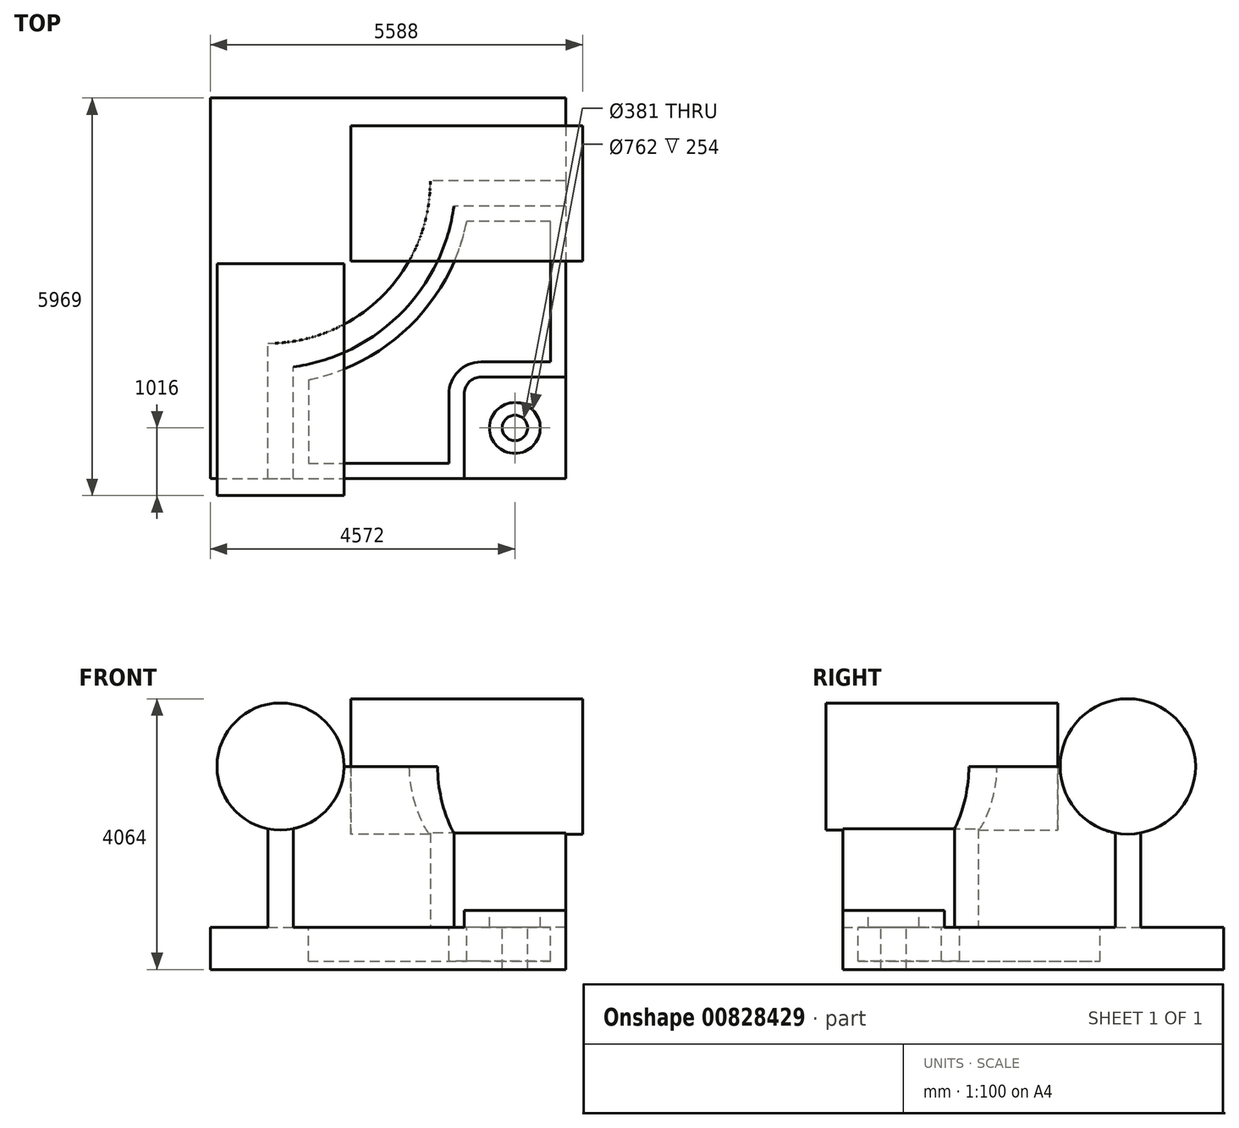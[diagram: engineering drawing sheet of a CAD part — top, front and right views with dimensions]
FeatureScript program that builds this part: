
annotation { "Feature Type Name" : "Feature", "Feature Type Description" : "" }
export const myFeature = defineFeature(function(context is Context, id is Id, definition is map)
    precondition{}
    {
        {
            var Q0;
            Q0=qCreatedBy(makeId("Top.planeOp"),FACE);
            var sketch = newSketch(context, id + "F0", { "sketchPlane" : qUnion([Q0])});
            skLineSegment(sketch, "E0.bottom", {"start": v(-2667, 2857.5) * mm, "end": v(2667, 2857.5) * mm});
            skLineSegment(sketch, "E0.top", {"start": v(-2667, -2857.5) * mm, "end": v(2667, -2857.5) * mm});
            skLineSegment(sketch, "E0.left", {"start": v(-2667, 2857.5) * mm, "end": v(-2667, -2857.5) * mm});
            skLineSegment(sketch, "E0.right", {"start": v(2667, 2857.5) * mm, "end": v(2667, -2857.5) * mm});
            skPoint(sketch, "E0.middle", {"position": v(0, 0) * mm});
            skSolve(sketch);
        }
        {
            var Q0;
            Q0=makeQuery(id+"F0.imprint","IMPRINT",FACE,{"disambiguationData":[TD([[makeQuery(id+"F0.imprint","IMPRINT",EDGE,{"derivedFrom":sQuery(id+"F0.wireOp",EDGE,"E0.bottom")}),-1.0]])]});
            extrude(context, id + "F1", {"entities" : qUnion([Q0]), "oppositeDirection" : true, "depth" : 635 * mm, "offsetDistance" : 25.4 * mm});
        }
        {
            var Q0;
            Q0=makeQuery(id+"F1.opExtrude","CAP_FACE",FACE,{"disambiguationData":[OSD([sQuery(id+"F0.wireOp",EDGE,"E0.bottom"),sQuery(id+"F0.wireOp",EDGE,"E0.top"),sQuery(id+"F0.wireOp",EDGE,"E0.left"),sQuery(id+"F0.wireOp",EDGE,"E0.right")])],"isStart":true});
            var sketch = newSketch(context, id + "F2", { "sketchPlane" : qUnion([Q0])});
            skLineSegment(sketch, "E1", {"start": v(-1803.4, -2857.5) * mm, "end": v(-1803.4, -825.5) * mm});
            skLineSegment(sketch, "E2", {"start": v(2667, 1612.9) * mm, "end": v(635, 1612.9) * mm});
            skArc(sketch, "E3", {"start": v(-1803.4, -825.5) * mm, "mid": v(-79.2, -111.3) * mm, "end": v(635, 1612.9) * mm});
            skLineSegment(sketch, "E4", {"start": v(-1803.4, 1612.9) * mm, "end": v(635, 1612.9) * mm, "construction": true});
            skLineSegment(sketch, "E5", {"start": v(-1803.4, 1612.9) * mm, "end": v(-1803.4, -825.5) * mm, "construction": true});
            skLineSegment(sketch, "E6.0", {"start": v(-1422.4, -2857.5) * mm, "end": v(-1422.4, -1180.64) * mm});
            skArc(sketch, "E6.1", {"start": v(-1422.4, -1180.64) * mm, "mid": v(190.22, -380.72) * mm, "end": v(990.14, 1231.9) * mm});
            skLineSegment(sketch, "E6.2", {"start": v(2667, 1231.9) * mm, "end": v(990.14, 1231.9) * mm});
            skLineSegment(sketch, "E7.0", {"start": v(2667, 2857.5) * mm, "end": v(2667, -2857.5) * mm});
            skLineSegment(sketch, "E8.0", {"start": v(-2667, -2857.5) * mm, "end": v(2667, -2857.5) * mm});
            skSolve(sketch);
        }
        {
            var Q0;
            {var subQ2=sQuery(id+"F2.wireOp",EDGE,"E1");Q0=makeQuery(id+"F2.imprint","IMPRINT",FACE,{"disambiguationData":[TD([[makeQuery(id+"F2.imprint","IMPRINT",EDGE,{"derivedFrom":subQ2}),-1.0]])]});}
            extrude(context, id + "F3", {"entities" : qUnion([Q0]), "operationType" : NewBodyOperationType.ADD, "depth" : 2413 * mm, "offsetDistance" : 25.4 * mm});
        }
        {
            var Q0;
            Q0=makeQuery(id+"F3.boolean.opBoolean","MERGE",FACE,{"derivedFrom":[makeQuery(id+"F1.opExtrude","SWEPT_FACE",FACE,{"disambiguationData":[OSD([sQuery(id+"F0.wireOp",EDGE,"E0.top")])]}),makeQuery(id+"F3.opExtrude","SWEPT_FACE",FACE,{"disambiguationData":[OSD([sQuery(id+"F2.wireOp",EDGE,"E8.0")])]})]});
            var sketch = newSketch(context, id + "F4", { "sketchPlane" : qUnion([Q0])});
            skCircle(sketch, "E9", {"center": v(-1612.9, 2413) * mm, "radius": 952.5 * mm});
            skSolve(sketch);
        }
        {
            var Q0;
            Q0 = qSketchRegion(id + "F4", true);
            extrude(context, id + "F5", {"entities" : qUnion([Q0]), "operationType" : NewBodyOperationType.ADD, "depth" : 254 * mm, "offsetDistance" : 25.4 * mm, "hasSecondDirection" : true, "secondDirectionOppositeDirection" : true, "secondDirectionDepth" : 3225.8 * mm});
        }
        {
            var Q0;
            Q0=makeQuery(id+"F3.boolean.opBoolean","MERGE",FACE,{"derivedFrom":[makeQuery(id+"F1.opExtrude","SWEPT_FACE",FACE,{"disambiguationData":[OSD([sQuery(id+"F0.wireOp",EDGE,"E0.right")])]}),makeQuery(id+"F3.opExtrude","SWEPT_FACE",FACE,{"disambiguationData":[OSD([sQuery(id+"F2.wireOp",EDGE,"E7.0")])]})]});
            var sketch = newSketch(context, id + "F6", { "sketchPlane" : qUnion([Q0])});
            skCircle(sketch, "E10", {"center": v(1422.4, 2413) * mm, "radius": 1016 * mm});
            skSolve(sketch);
        }
        {
            var Q0;
            Q0 = qSketchRegion(id + "F6", true);
            extrude(context, id + "F7", {"entities" : qUnion([Q0]), "operationType" : NewBodyOperationType.ADD, "depth" : 254 * mm, "offsetDistance" : 25.4 * mm, "hasSecondDirection" : true, "secondDirectionOppositeDirection" : true, "secondDirectionDepth" : 3225.8 * mm});
        }
        {
            var Q0;
            {var subQ0=sQuery(id+"F0.wireOp",EDGE,"E0.right");var subQ1=sQuery(id+"F0.wireOp",EDGE,"E0.top");Q0=makeQuery(id+"F3.boolean.opBoolean","SPLIT",FACE,{"disambiguationData":[TD([makeQuery(id+"F3.opExtrude","SWEPT_FACE",FACE,{"disambiguationData":[OSD([sQuery(id+"F2.wireOp",EDGE,"E6.0")])]})])],"derivedFrom":makeQuery(id+"F1.opExtrude","CAP_FACE",FACE,{"disambiguationData":[OSD([sQuery(id+"F0.wireOp",EDGE,"E0.bottom"),subQ1,sQuery(id+"F0.wireOp",EDGE,"E0.left"),subQ0])],"isStart":true})});}
            var sketch = newSketch(context, id + "F8", { "sketchPlane" : qUnion([Q0])});
            skLineSegment(sketch, "E11.bottom", {"start": v(2667, -2857.5) * mm, "end": v(1143, -2857.5) * mm});
            skLineSegment(sketch, "E11.top", {"start": v(2667, -1333.5) * mm, "end": v(1143, -1333.5) * mm});
            skLineSegment(sketch, "E11.left", {"start": v(2667, -2857.5) * mm, "end": v(2667, -1333.5) * mm});
            skLineSegment(sketch, "E11.right", {"start": v(1143, -2857.5) * mm, "end": v(1143, -1333.5) * mm});
            skSolve(sketch);
        }
        {
            var Q0;
            Q0 = qSketchRegion(id + "F8", true);
            extrude(context, id + "F9", {"entities" : qUnion([Q0]), "operationType" : NewBodyOperationType.ADD, "depth" : 254 * mm, "offsetDistance" : 25.4 * mm});
        }
        {
            var Q0;
            Q0=makeQuery(id+"F9.opExtrude","SWEPT_EDGE",EDGE,{"disambiguationData":[OSD([sQuery(id+"F8.wireOp",EDGE,"E11.top"),sQuery(id+"F8.wireOp",EDGE,"E11.right")])]});
            fillet(context, id + "F10", {"entities" : qUnion([Q0]), "radius" : 254 * mm, "tangentPropagation" : true, "allowEdgeOverflow" : false});
        }
        {
            var Q0;
            {var subQ0=sQuery(id+"F0.wireOp",EDGE,"E0.right");var subQ1=sQuery(id+"F0.wireOp",EDGE,"E0.top");Q0=makeQuery(id+"F3.boolean.opBoolean","SPLIT",FACE,{"disambiguationData":[TD([makeQuery(id+"F3.opExtrude","SWEPT_FACE",FACE,{"disambiguationData":[OSD([sQuery(id+"F2.wireOp",EDGE,"E6.0")])]})])],"derivedFrom":makeQuery(id+"F1.opExtrude","CAP_FACE",FACE,{"disambiguationData":[OSD([sQuery(id+"F0.wireOp",EDGE,"E0.bottom"),subQ1,sQuery(id+"F0.wireOp",EDGE,"E0.left"),subQ0])],"isStart":true})});}
            var sketch = newSketch(context, id + "F11", { "sketchPlane" : qUnion([Q0])});
            skLineSegment(sketch, "E12.0", {"start": v(-1193.8, -1373.52) * mm, "end": v(-1193.8, -2628.9) * mm});
            skArc(sketch, "E12.1", {"start": v(1183.02, 1003.3) * mm, "mid": v(351.86, -542.36) * mm, "end": v(-1193.8, -1373.52) * mm});
            skLineSegment(sketch, "E12.2", {"start": v(-1193.8, -2628.9) * mm, "end": v(914.4, -2628.9) * mm});
            skLineSegment(sketch, "E12.3", {"start": v(2438.4, 1003.3) * mm, "end": v(1183.02, 1003.3) * mm});
            skLineSegment(sketch, "E12.4", {"start": v(914.4, -2628.9) * mm, "end": v(914.4, -1587.5) * mm});
            skArc(sketch, "E12.5", {"start": v(914.4, -1587.5) * mm, "mid": v(1055.75, -1246.25) * mm, "end": v(1397, -1104.9) * mm});
            skLineSegment(sketch, "E12.6", {"start": v(1397, -1104.9) * mm, "end": v(2438.4, -1104.9) * mm});
            skLineSegment(sketch, "E12.7", {"start": v(2438.4, -1104.9) * mm, "end": v(2438.4, 1003.3) * mm});
            skSolve(sketch);
        }
        {
            var Q0;
            Q0=makeQuery(id+"F11.imprint","IMPRINT",FACE,{"disambiguationData":[TD([[makeQuery(id+"F11.imprint","IMPRINT",EDGE,{"derivedFrom":sQuery(id+"F11.wireOp",EDGE,"E12.0")}),1.0]])]});
            extrude(context, id + "F12", {"entities" : qUnion([Q0]), "operationType" : NewBodyOperationType.REMOVE, "oppositeDirection" : true, "depth" : 508 * mm, "offsetDistance" : 25.4 * mm});
        }
        {
            var Q0;
            Q0=makeQuery(id+"F9.opExtrude","CAP_FACE",FACE,{"disambiguationData":[OSD([sQuery(id+"F8.wireOp",EDGE,"E11.bottom"),sQuery(id+"F8.wireOp",EDGE,"E11.top"),sQuery(id+"F8.wireOp",EDGE,"E11.left"),sQuery(id+"F8.wireOp",EDGE,"E11.right")])],"isStart":false});
            var sketch = newSketch(context, id + "F13", { "sketchPlane" : qUnion([Q0])});
            skCircle(sketch, "E13", {"center": v(1905, -2095.5) * mm, "radius": 381 * mm});
            skSolve(sketch);
        }
        {
            var Q0;
            Q0=sQuery(id+"F13.wireOp",VERTEX,"E13.center");
            var Q1;
            Q1=makeQuery(id+"F1.opExtrude","SWEPT_BODY",BODY,{"disambiguationData":[OSD([sQuery(id+"F0.wireOp",EDGE,"E0.bottom"),sQuery(id+"F0.wireOp",EDGE,"E0.top"),sQuery(id+"F0.wireOp",EDGE,"E0.left"),sQuery(id+"F0.wireOp",EDGE,"E0.right")])]});
            hole(context, id + "F14", {"style" : HoleStyle.C_BORE, "endStyle" : HoleEndStyle.THROUGH, "holeDiameter" : 381 * mm, "cBoreDiameter" : 762 * mm, "cBoreDepth" : 254 * mm, "majorDiameter" : 6.35 * mm, "isTappedThrough" : true, "tappedDepth" : 12.7 * mm, "tapClearance" : 3, "locations" : qUnion([Q0]), "scope" : qUnion([Q1])});
        }
    });
